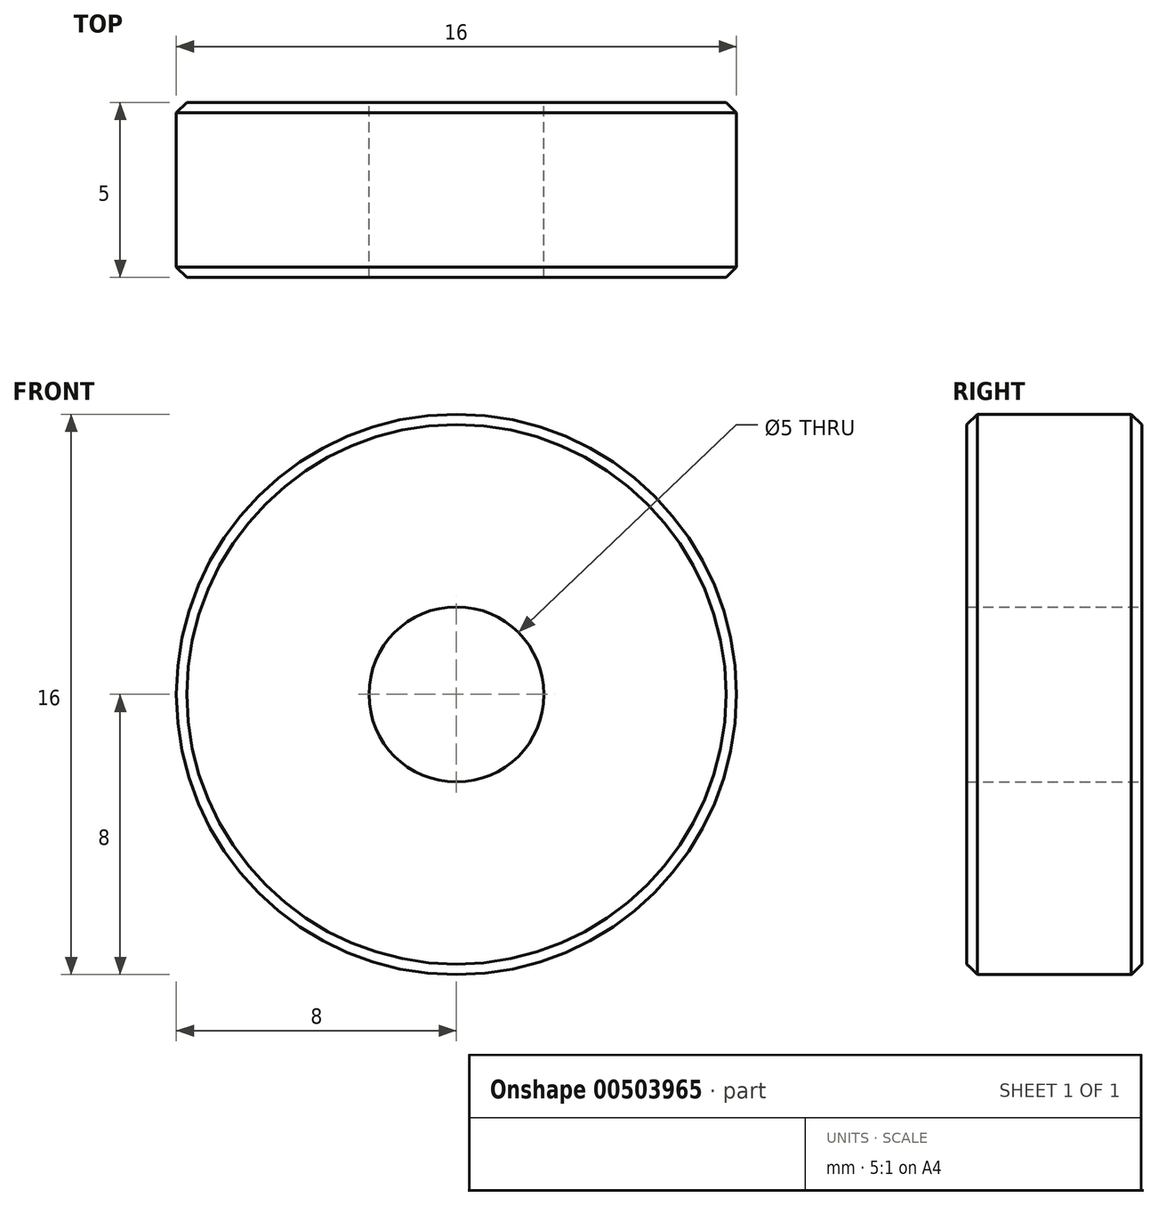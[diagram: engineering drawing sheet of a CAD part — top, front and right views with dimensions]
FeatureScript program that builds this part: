
annotation { "Feature Type Name" : "Feature", "Feature Type Description" : "" }
export const myFeature = defineFeature(function(context is Context, id is Id, definition is map)
    precondition{}
    {
        {
            var Q0;
            Q0=qCreatedBy(makeId("Front.planeOp"),FACE);
            var sketch = newSketch(context, id + "F0", { "sketchPlane" : qUnion([Q0])});
            skCircle(sketch, "E0", {"center": v(0, 0) * mm, "radius": 8 * mm});
            skCircle(sketch, "E1", {"center": v(0, 0) * mm, "radius": 2.5 * mm});
            skSolve(sketch);
        }
        {
            var Q0;
            Q0=makeQuery(id+"F0.imprint","IMPRINT",FACE,{"disambiguationData":[TD([[makeQuery(id+"F0.imprint","IMPRINT",EDGE,{"derivedFrom":sQuery(id+"F0.wireOp",EDGE,"E0")}),1.0]])]});
            extrude(context, id + "F1", {"entities" : qUnion([Q0]), "depth" : 5 * mm, "offsetDistance" : 25 * mm});
        }
        {
            var Q0;
            Q0=makeQuery(id+"F1.opExtrude","CAP_EDGE",EDGE,{"disambiguationData":[OSD([sQuery(id+"F0.wireOp",EDGE,"E0")])],"isStart":true});
            var Q1;
            Q1=makeQuery(id+"F1.opExtrude","CAP_EDGE",EDGE,{"disambiguationData":[OSD([sQuery(id+"F0.wireOp",EDGE,"E0")])],"isStart":false});
            chamfer(context, id + "F2", {"entities" : qUnion([Q0, Q1]), "width" : .3 * mm, "tangentPropagation" : true});
        }
    });
